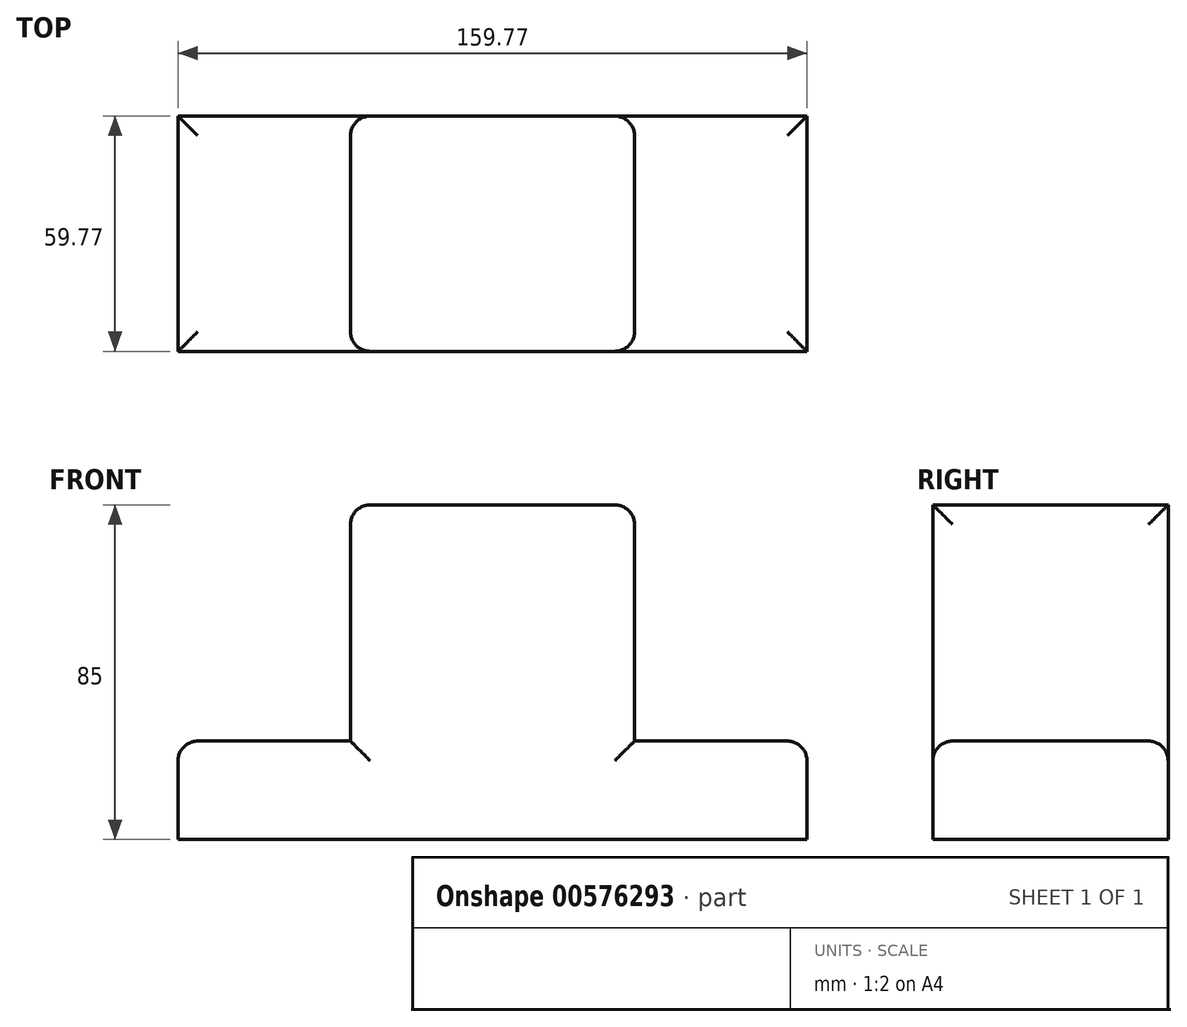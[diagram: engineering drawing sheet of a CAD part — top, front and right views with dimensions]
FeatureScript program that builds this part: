
annotation { "Feature Type Name" : "Feature", "Feature Type Description" : "" }
export const myFeature = defineFeature(function(context is Context, id is Id, definition is map)
    precondition{}
    {
        {
            var Q0;
            Q0=qCreatedBy(makeId("Top.planeOp"),FACE);
            var sketch = newSketch(context, id + "F0", { "sketchPlane" : qUnion([Q0])});
            skLineSegment(sketch, "E0.bottom", {"start": v(-67.67, 35.52) * mm, "end": v(92.1, 35.52) * mm});
            skLineSegment(sketch, "E0.top", {"start": v(-67.67, -24.25) * mm, "end": v(92.1, -24.25) * mm});
            skLineSegment(sketch, "E0.left", {"start": v(-67.67, 35.52) * mm, "end": v(-67.67, -24.25) * mm});
            skLineSegment(sketch, "E0.right", {"start": v(92.1, 35.52) * mm, "end": v(92.1, -24.25) * mm});
            skSolve(sketch);
        }
        {
            var Q0;
            Q0 = qSketchRegion(id + "F0", true);
            extrude(context, id + "F1", {"entities" : qUnion([Q0]), "depth" : 25 * mm, "offsetDistance" : 25 * mm});
        }
        {
            var Q0;
            Q0=makeQuery(id+"F1.opExtrude","CAP_FACE",FACE,{"disambiguationData":[OSD([sQuery(id+"F0.wireOp",EDGE,"E0.bottom"),sQuery(id+"F0.wireOp",EDGE,"E0.top"),sQuery(id+"F0.wireOp",EDGE,"E0.left"),sQuery(id+"F0.wireOp",EDGE,"E0.right")])],"isStart":false});
            var sketch = newSketch(context, id + "F2", { "sketchPlane" : qUnion([Q0])});
            skLineSegment(sketch, "E1.bottom", {"start": v(12.22, 35.52) * mm, "end": v(-23.87, 35.52) * mm});
            skLineSegment(sketch, "E1.top", {"start": v(12.22, -24.25) * mm, "end": v(-23.87, -24.25) * mm});
            skLineSegment(sketch, "E1.left", {"start": v(12.22, 35.52) * mm, "end": v(12.22, -24.25) * mm});
            skLineSegment(sketch, "E1.right", {"start": v(-23.87, 35.52) * mm, "end": v(-23.87, -24.25) * mm});
            skLineSegment(sketch, "E2.bottom", {"start": v(12.22, 35.52) * mm, "end": v(48.3, 35.52) * mm});
            skLineSegment(sketch, "E2.top", {"start": v(12.22, -24.25) * mm, "end": v(48.3, -24.25) * mm});
            skLineSegment(sketch, "E2.right", {"start": v(48.3, 35.52) * mm, "end": v(48.3, -24.25) * mm});
            skLineSegment(sketch, "E3.bottom", {"start": v(-23.87, 35.52) * mm, "end": v(48.3, 35.52) * mm});
            skLineSegment(sketch, "E3.top", {"start": v(-23.87, -24.25) * mm, "end": v(48.3, -24.25) * mm});
            skSolve(sketch);
        }
        {
            var Q0;
            Q0 = qSketchRegion(id + "F2", true);
            extrude(context, id + "F3", {"entities" : qUnion([Q0]), "operationType" : NewBodyOperationType.ADD, "depth" : 60 * mm, "offsetDistance" : 25 * mm});
        }
        {
            var Q0;
            Q0=makeQuery(id+"F3.opExtrude","SWEPT_EDGE",EDGE,{"disambiguationData":[OSD([sQuery(id+"F0.wireOp",EDGE,"E0.top"),sQuery(id+"F2.wireOp",EDGE,"E3.top"),sQuery(id+"F2.wireOp",EDGE,"E1.right")])]});
            var Q1;
            Q1=makeQuery(id+"F3.opExtrude","SWEPT_EDGE",EDGE,{"disambiguationData":[OSD([sQuery(id+"F0.wireOp",EDGE,"E0.bottom"),sQuery(id+"F2.wireOp",EDGE,"E3.bottom"),sQuery(id+"F2.wireOp",EDGE,"E1.right")])]});
            var Q2;
            Q2=makeQuery(id+"F3.opExtrude","SWEPT_EDGE",EDGE,{"disambiguationData":[OSD([sQuery(id+"F0.wireOp",EDGE,"E0.top"),sQuery(id+"F2.wireOp",EDGE,"E3.top"),sQuery(id+"F2.wireOp",EDGE,"E2.right")])]});
            var Q3;
            {var subQ0=sQuery(id+"F0.wireOp",EDGE,"E0.left");var subQ1=sQuery(id+"F0.wireOp",EDGE,"E0.top");Q3=makeQuery(id+"F3.boolean.opBoolean","SPLIT",EDGE,{"disambiguationData":[TD([makeQuery(id+"F1.opExtrude","SWEPT_FACE",FACE,{"disambiguationData":[OSD([subQ0])]})])],"derivedFrom":makeQuery(id+"F1.opExtrude","CAP_EDGE",EDGE,{"disambiguationData":[OSD([subQ1])],"isStart":false})});}
            var Q4;
            {var subQ0=sQuery(id+"F0.wireOp",EDGE,"E0.left");var subQ1=sQuery(id+"F0.wireOp",EDGE,"E0.bottom");Q4=makeQuery(id+"F3.boolean.opBoolean","SPLIT",EDGE,{"disambiguationData":[TD([makeQuery(id+"F1.opExtrude","SWEPT_FACE",FACE,{"disambiguationData":[OSD([subQ0])]})])],"derivedFrom":makeQuery(id+"F1.opExtrude","CAP_EDGE",EDGE,{"disambiguationData":[OSD([subQ1])],"isStart":false})});}
            var Q5;
            {var subQ0=sQuery(id+"F0.wireOp",EDGE,"E0.right");var subQ1=sQuery(id+"F0.wireOp",EDGE,"E0.top");Q5=makeQuery(id+"F3.boolean.opBoolean","SPLIT",EDGE,{"disambiguationData":[TD([makeQuery(id+"F1.opExtrude","SWEPT_FACE",FACE,{"disambiguationData":[OSD([subQ0])]})])],"derivedFrom":makeQuery(id+"F1.opExtrude","CAP_EDGE",EDGE,{"disambiguationData":[OSD([subQ1])],"isStart":false})});}
            var Q6;
            {var subQ0=sQuery(id+"F0.wireOp",EDGE,"E0.right");var subQ1=sQuery(id+"F0.wireOp",EDGE,"E0.bottom");Q6=makeQuery(id+"F3.boolean.opBoolean","SPLIT",EDGE,{"disambiguationData":[TD([makeQuery(id+"F1.opExtrude","SWEPT_FACE",FACE,{"disambiguationData":[OSD([subQ0])]})])],"derivedFrom":makeQuery(id+"F1.opExtrude","CAP_EDGE",EDGE,{"disambiguationData":[OSD([subQ1])],"isStart":false})});}
            var Q7;
            Q7=makeQuery(id+"F3.opExtrude","SWEPT_EDGE",EDGE,{"disambiguationData":[OSD([sQuery(id+"F0.wireOp",EDGE,"E0.bottom"),sQuery(id+"F2.wireOp",EDGE,"E3.bottom"),sQuery(id+"F2.wireOp",EDGE,"E2.right")])]});
            var Q8;
            Q8=makeQuery(id+"F1.opExtrude","CAP_EDGE",EDGE,{"disambiguationData":[OSD([sQuery(id+"F0.wireOp",EDGE,"E0.left")])],"isStart":false});
            var Q9;
            Q9=makeQuery(id+"F1.opExtrude","CAP_EDGE",EDGE,{"disambiguationData":[OSD([sQuery(id+"F0.wireOp",EDGE,"E0.right")])],"isStart":false});
            var Q10;
            Q10=makeQuery(id+"F3.opExtrude","CAP_EDGE",EDGE,{"disambiguationData":[OSD([sQuery(id+"F2.wireOp",EDGE,"E2.right")])],"isStart":false});
            var Q11;
            Q11=makeQuery(id+"F3.opExtrude","CAP_EDGE",EDGE,{"disambiguationData":[OSD([sQuery(id+"F2.wireOp",EDGE,"E1.right")])],"isStart":false});
            var Q12;
            Q12=makeQuery(id+"F3.opExtrude","CAP_EDGE",EDGE,{"disambiguationData":[OSD([sQuery(id+"F2.wireOp",EDGE,"E3.bottom")])],"isStart":false});
            var Q13;
            Q13=makeQuery(id+"F3.opExtrude","CAP_EDGE",EDGE,{"disambiguationData":[OSD([sQuery(id+"F2.wireOp",EDGE,"E3.top")])],"isStart":false});
            fillet(context, id + "F4", {"entities" : qUnion([Q0, Q1, Q2, Q3, Q4, Q5, Q6, Q7, Q8, Q9, Q10, Q11, Q12, Q13]), "radius" : 5 * mm, "tangentPropagation" : true, "allowEdgeOverflow" : false});
        }
    });
